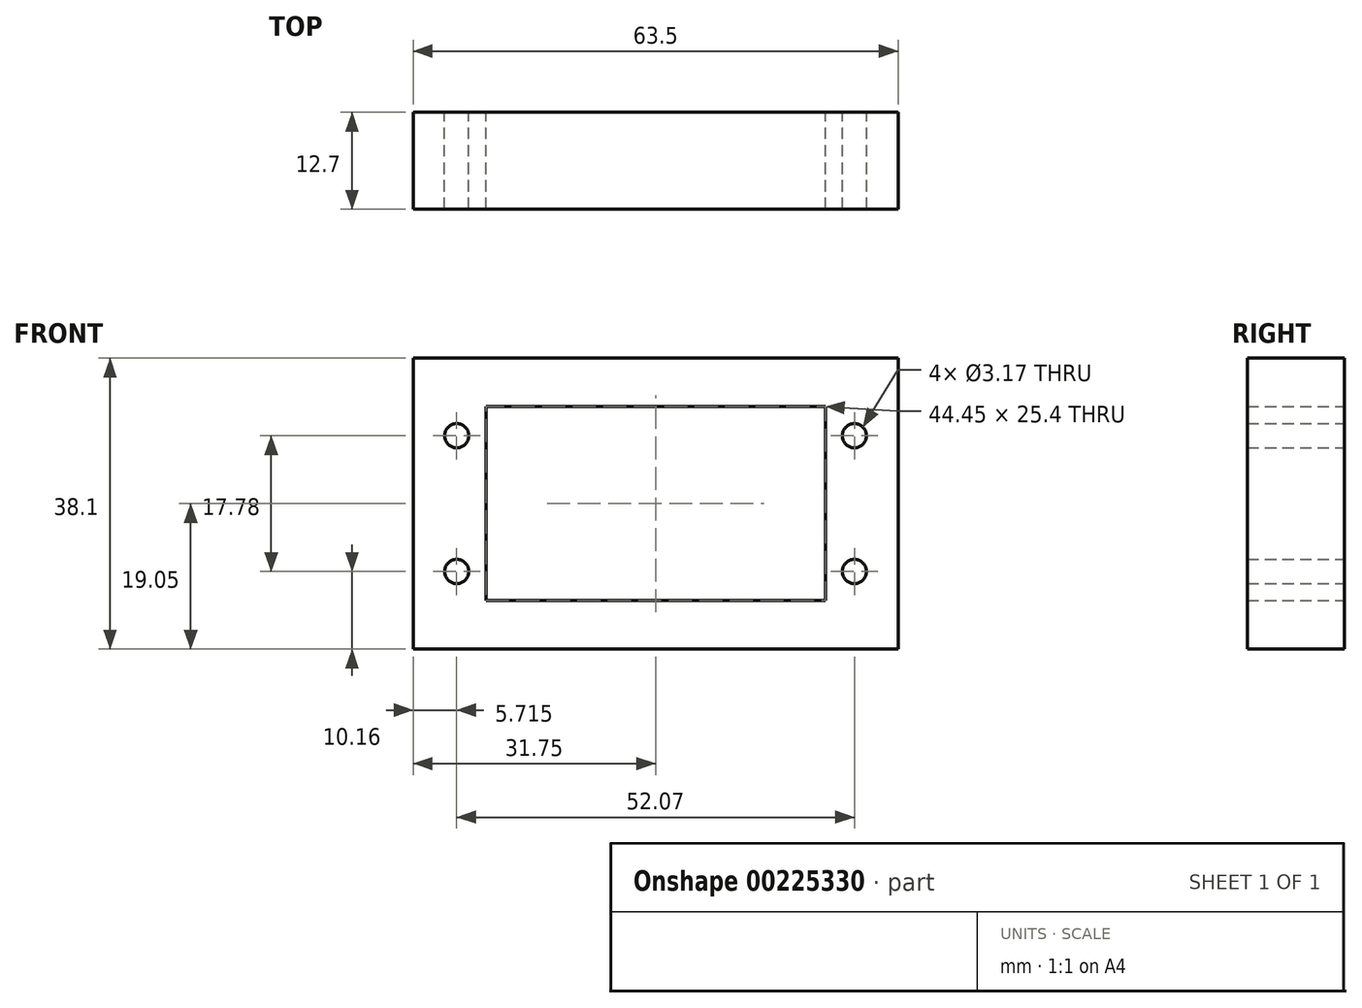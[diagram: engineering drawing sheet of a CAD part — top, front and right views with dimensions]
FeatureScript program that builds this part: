
annotation { "Feature Type Name" : "Feature", "Feature Type Description" : "" }
export const myFeature = defineFeature(function(context is Context, id is Id, definition is map)
    precondition{}
    {
        {
            var Q0;
            Q0=qCreatedBy(makeId("Front.planeOp"),FACE);
            var sketch = newSketch(context, id + "F0", { "sketchPlane" : qUnion([Q0])});
            skLineSegment(sketch, "E0.bottom", {"start": v(0, 0) * mm, "end": v(63.5, 0) * mm});
            skLineSegment(sketch, "E0.top", {"start": v(0, 38.1) * mm, "end": v(63.5, 38.1) * mm});
            skLineSegment(sketch, "E0.left", {"start": v(0, 0) * mm, "end": v(0, 38.1) * mm});
            skLineSegment(sketch, "E0.right", {"start": v(63.5, 0) * mm, "end": v(63.5, 38.1) * mm});
            skCircle(sketch, "E1", {"center": v(5.71, 27.94) * mm, "radius": 1.59 * mm});
            skCircle(sketch, "E2", {"center": v(57.79, 27.94) * mm, "radius": 1.59 * mm});
            skCircle(sketch, "E3", {"center": v(57.79, 10.16) * mm, "radius": 1.59 * mm});
            skCircle(sketch, "E4", {"center": v(5.71, 10.16) * mm, "radius": 1.59 * mm});
            skPoint(sketch, "E5.start.orphan", {"position": v(31.75, 27.94) * mm});
            skPoint(sketch, "E6.end.orphan", {"position": v(5.72, 19.05) * mm});
            skPoint(sketch, "E6.start.orphan", {"position": v(0, 19.05) * mm});
            skPoint(sketch, "E7.end.orphan", {"position": v(31.19, 0) * mm});
            skPoint(sketch, "E7.start.orphan", {"position": v(31.75, 10.16) * mm});
            skPoint(sketch, "E8.end.orphan", {"position": v(63.5, 19.05) * mm});
            skPoint(sketch, "E9.orphan", {"position": v(57.79, 19.05) * mm});
            skLineSegment(sketch, "E10.bottom", {"start": v(9.52, 31.75) * mm, "end": v(53.98, 31.75) * mm});
            skLineSegment(sketch, "E10.top", {"start": v(9.52, 6.35) * mm, "end": v(53.98, 6.35) * mm});
            skLineSegment(sketch, "E10.left", {"start": v(9.52, 31.75) * mm, "end": v(9.52, 6.35) * mm});
            skLineSegment(sketch, "E10.right", {"start": v(53.97, 31.75) * mm, "end": v(53.97, 6.35) * mm});
            skPoint(sketch, "E11.start.orphan", {"position": v(31.75, 38.1) * mm});
            skSolve(sketch);
        }
        {
            var Q0;
            Q0 = qSketchRegion(id + "F0", true);
            extrude(context, id + "F1", {"entities" : qUnion([Q0]), "depth" : 12.7 * mm});
        }
    });
